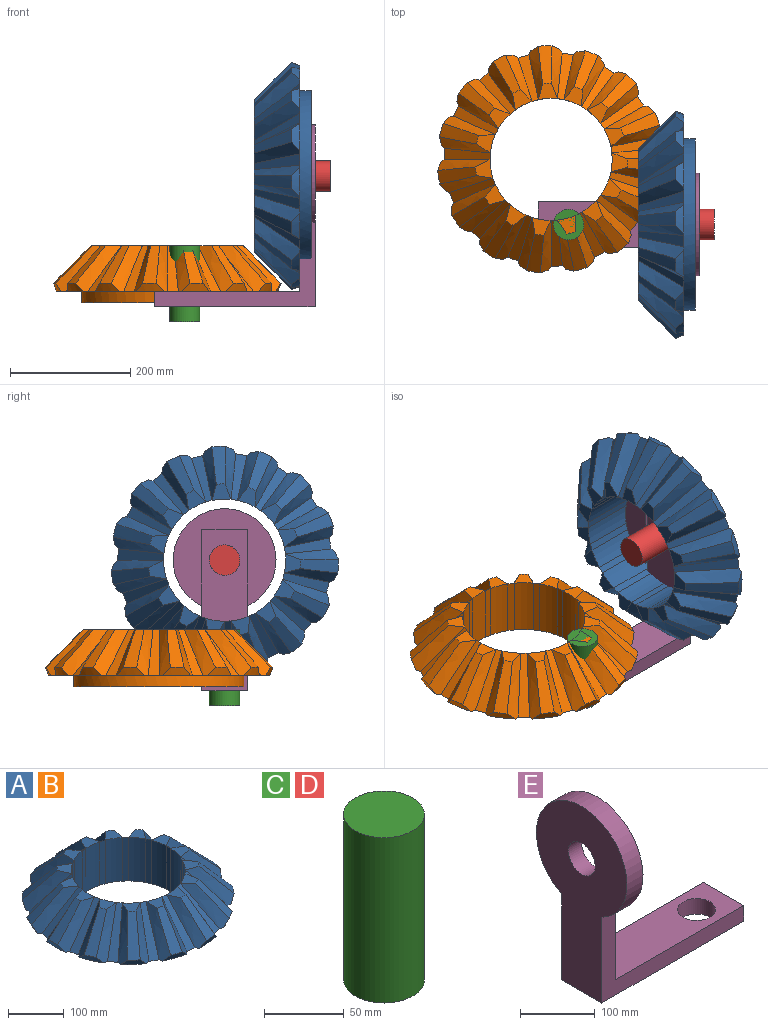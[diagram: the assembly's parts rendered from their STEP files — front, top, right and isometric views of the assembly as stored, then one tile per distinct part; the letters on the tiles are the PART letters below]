
ASSEMBLY  parts=5 mates=5
PART A: 123 faces, bbox 408.6x408.6x95.3 mm
  f0: plane 31.03x30.54mm, normal (0,0,1), area 585.2mm2, adj f44,f46,f50,f92
  f1: plane 31.03x30.54mm, normal (0,0,1), area 585.2mm2, adj f16,f47,f88,f94
  f2: plane 34.9x34.21mm, normal (0,0,1), area 585.2mm2, adj f18,f85,f89,f96
  f3: plane 34.36x33.22mm, normal (0,0,1), area 585.2mm2, adj f20,f82,f86,f98
  f4: plane 31.55x28.57mm, normal (0,0,1), area 585.2mm2, adj f22,f79,f83,f100
  f5: plane 32.17x30.17mm, normal (0,0,1), area 585.2mm2, adj f24,f76,f80,f102
  f6: plane 35.05x34.82mm, normal (0,0,1), area 585.2mm2, adj f26,f73,f77,f104
  f7: plane 33.45x31.87mm, normal (0,0,1), area 585.2mm2, adj f28,f70,f74,f106
  f8: plane 31.72x26.5mm, normal (0,0,1), area 585.2mm2, adj f30,f67,f71,f108
  f9: plane 33.45x31.87mm, normal (0,0,1), area 585.2mm2, adj f32,f64,f68,f110
  f10: plane 35.05x34.82mm, normal (0,0,1), area 585.2mm2, adj f34,f61,f65,f112
  f11: plane 32.17x30.17mm, normal (0,0,1), area 585.2mm2, adj f36,f58,f62,f114
  f12: plane 31.55x28.57mm, normal (0,0,1), area 585.2mm2, adj f38,f55,f59,f116
  f13: plane 34.36x33.22mm, normal (0,0,1), area 585.2mm2, adj f40,f52,f56,f118
  f14: plane 34.9x34.21mm, normal (0,0,1), area 585.2mm2, adj f42,f49,f53,f120
  f15: plane 368.3x367.72mm, normal (0,0,-1), area 40460.3mm2, adj f17,f19,f21,f23,f25,f27,f29,f31
  f16: cone r=203.2mm half-angle=45deg, axis (0,0,-1), area 1668.1mm2, adj f1,f17,f47,f88
  f17: cone r=189.73mm half-angle=22.5deg, axis (0,0,1), area 520mm2, adj f15,f16,f47,f88
  f18: cone r=203.2mm half-angle=45deg, axis (0,0,-1), area 1668.1mm2, adj f2,f19,f85,f89
  f19: cone r=189.73mm half-angle=22.5deg, axis (0,0,1), area 520mm2, adj f15,f18,f85,f89
  f20: cone r=203.2mm half-angle=45deg, axis (0,0,-1), area 1668.1mm2, adj f3,f21,f82,f86
  f21: cone r=189.73mm half-angle=22.5deg, axis (0,0,1), area 520mm2, adj f15,f20,f82,f86
  f22: cone r=203.2mm half-angle=45deg, axis (0,0,-1), area 1668.1mm2, adj f4,f23,f79,f83
  f23: cone r=189.73mm half-angle=22.5deg, axis (0,0,1), area 520mm2, adj f15,f22,f79,f83
  f24: cone r=203.2mm half-angle=45deg, axis (0,0,-1), area 1668.1mm2, adj f5,f25,f76,f80
  f25: cone r=189.73mm half-angle=22.5deg, axis (0,0,1), area 520mm2, adj f15,f24,f76,f80
  f26: cone r=203.2mm half-angle=45deg, axis (0,0,-1), area 1668.1mm2, adj f6,f27,f73,f77
  f27: cone r=189.73mm half-angle=22.5deg, axis (0,0,1), area 520mm2, adj f15,f26,f73,f77
  f28: cone r=203.2mm half-angle=45deg, axis (0,0,-1), area 1668.1mm2, adj f7,f29,f70,f74
  f29: cone r=189.73mm half-angle=22.5deg, axis (0,0,1), area 520mm2, adj f15,f28,f70,f74
  f30: cone r=203.2mm half-angle=45deg, axis (0,0,-1), area 1668.1mm2, adj f8,f31,f67,f71
  f31: cone r=189.73mm half-angle=22.5deg, axis (0,0,1), area 520mm2, adj f15,f30,f67,f71
  f32: cone r=203.2mm half-angle=45deg, axis (0,0,-1), area 1668.1mm2, adj f9,f33,f64,f68
  f33: cone r=189.73mm half-angle=22.5deg, axis (0,0,1), area 520mm2, adj f15,f32,f64,f68
  f34: cone r=203.2mm half-angle=45deg, axis (0,0,-1), area 1668.1mm2, adj f10,f35,f61,f65
  f35: cone r=189.73mm half-angle=22.5deg, axis (0,0,1), area 520mm2, adj f15,f34,f61,f65
  f36: cone r=203.2mm half-angle=45deg, axis (0,0,-1), area 1668.1mm2, adj f11,f37,f58,f62
  f37: cone r=189.73mm half-angle=22.5deg, axis (0,0,1), area 520mm2, adj f15,f36,f58,f62
  f38: cone r=203.2mm half-angle=45deg, axis (0,0,-1), area 1668.1mm2, adj f12,f39,f55,f59
  f39: cone r=189.73mm half-angle=22.5deg, axis (0,0,1), area 520mm2, adj f15,f38,f55,f59
  f40: cone r=203.2mm half-angle=45deg, axis (0,0,-1), area 1668.1mm2, adj f13,f41,f52,f56
  f41: cone r=189.73mm half-angle=22.5deg, axis (0,0,1), area 520mm2, adj f15,f40,f52,f56
  f42: cone r=203.2mm half-angle=45deg, axis (0,0,-1), area 1668.1mm2, adj f14,f43,f49,f53
  f43: cone r=189.73mm half-angle=22.5deg, axis (0,0,1), area 520mm2, adj f15,f42,f49,f53
  f44: cone r=203.2mm half-angle=45deg, axis (0,0,-1), area 1668.1mm2, adj f0,f45,f46,f50
  f45: cone r=189.73mm half-angle=22.5deg, axis (0,0,1), area 520mm2, adj f15,f44,f46,f50
  f46: bspline ~101.6x76.2mm, area 2318.6mm2, adj f0,f15,f44,f45,f48
  f47: bspline ~99.08x76.2mm, area 2314.1mm2, adj f1,f15,f16,f17,f48
  f48: plane 76.2x76.2mm, normal (0.71,0,0.71), area 1594.3mm2, adj f15,f46,f47,f93
  f49: bspline ~81.96x76.2mm, area 2318.6mm2, adj f14,f15,f42,f43,f51
  f50: bspline ~103.67x76.2mm, area 2314.1mm2, adj f0,f15,f44,f45,f51
  f51: plane 76.2x75.63mm, normal (0.65,-0.29,0.71), area 1594.3mm2, adj f15,f49,f50,f91
  f52: bspline ~93.36x76.2mm, area 2318.6mm2, adj f13,f15,f40,f41,f54
  f53: bspline ~87.82x76.2mm, area 2314.1mm2, adj f14,f15,f42,f43,f54
  f54: plane 76.2x66.53mm, normal (0.47,-0.53,0.71), area 1594.3mm2, adj f15,f52,f53,f119
  f55: bspline ~104.88x76.2mm, area 2318.6mm2, adj f12,f15,f38,f39,f57
  f56: bspline ~86.68x76.2mm, area 2314.1mm2, adj f13,f15,f40,f41,f57
  f57: plane 77.04x76.2mm, normal (0.22,-0.67,0.71), area 1594.3mm2, adj f15,f55,f56,f117
  f58: bspline ~98.25x76.2mm, area 2318.6mm2, adj f11,f15,f36,f37,f60
  f59: bspline ~103.83x76.2mm, area 2314.1mm2, adj f12,f15,f38,f39,f60
  f60: plane 77.33x76.2mm, normal (-0.07,-0.7,0.71), area 1594.3mm2, adj f15,f58,f59,f115
  f61: bspline ~76.2x74.64mm, area 2318.6mm2, adj f10,f15,f34,f35,f63
  f62: bspline ~101.33x76.2mm, area 2314.1mm2, adj f11,f15,f36,f37,f63
  f63: plane 76.2x73.39mm, normal (-0.35,-0.61,0.71), area 1594.3mm2, adj f15,f61,f62,f113
  f64: bspline ~97.89x76.2mm, area 2318.6mm2, adj f9,f15,f32,f33,f66
  f65: bspline ~81.31x76.2mm, area 2314.1mm2, adj f10,f15,f34,f35,f66
  f66: plane 76.2x70.34mm, normal (-0.57,-0.42,0.71), area 1594.3mm2, adj f15,f64,f65,f111
  f67: bspline ~104.93x76.2mm, area 2318.6mm2, adj f8,f15,f30,f31,f69
  f68: bspline ~93.83x76.2mm, area 2314.1mm2, adj f9,f15,f32,f33,f69
  f69: plane 77.61x76.2mm, normal (-0.69,-0.15,0.71), area 1594.3mm2, adj f15,f67,f68,f109
  f70: bspline ~93.83x76.2mm, area 2318.6mm2, adj f7,f15,f28,f29,f72
  f71: bspline ~104.93x76.2mm, area 2314.1mm2, adj f8,f15,f30,f31,f72
  f72: plane 77.61x76.2mm, normal (-0.69,0.15,0.71), area 1594.3mm2, adj f15,f70,f71,f107
  f73: bspline ~81.31x76.2mm, area 2318.6mm2, adj f6,f15,f26,f27,f75
  f74: bspline ~97.89x76.2mm, area 2314.1mm2, adj f7,f15,f28,f29,f75
  f75: plane 76.2x70.34mm, normal (-0.57,0.42,0.71), area 1594.3mm2, adj f15,f73,f74,f105
  f76: bspline ~98.03x76.2mm, area 2318.6mm2, adj f5,f15,f24,f25,f78
  f77: bspline ~76.2x74.64mm, area 2314.1mm2, adj f6,f15,f26,f27,f78
  f78: plane 76.2x73.39mm, normal (-0.35,0.61,0.71), area 1594.3mm2, adj f15,f76,f77,f103
  f79: bspline ~101.1x76.2mm, area 2318.6mm2, adj f4,f15,f22,f23,f81
  f80: bspline ~98.25x76.2mm, area 2314.1mm2, adj f5,f15,f24,f25,f81
  f81: plane 77.33x76.2mm, normal (-0.07,0.7,0.71), area 1594.3mm2, adj f15,f79,f80,f101
  f82: bspline ~86.68x76.2mm, area 2318.6mm2, adj f3,f15,f20,f21,f84
  f83: bspline ~104.88x76.2mm, area 2314.1mm2, adj f4,f15,f22,f23,f84
  f84: plane 77.04x76.2mm, normal (0.22,0.67,0.71), area 1594.3mm2, adj f15,f82,f83,f99
  f85: bspline ~87.82x76.2mm, area 2318.6mm2, adj f2,f15,f18,f19,f87
  f86: bspline ~93.36x76.2mm, area 2314.1mm2, adj f3,f15,f20,f21,f87
  f87: plane 76.2x66.53mm, normal (0.47,0.53,0.71), area 1594.3mm2, adj f15,f85,f86,f97
  f88: bspline ~103.67x76.2mm, area 2318.6mm2, adj f1,f15,f16,f17,f90
  f89: bspline ~81.96x76.2mm, area 2314.1mm2, adj f2,f15,f18,f19,f90
  f90: plane 76.2x75.63mm, normal (0.65,0.29,0.71), area 1594.3mm2, adj f15,f88,f89,f95
  f91: plane 95.25x9.83mm, normal (-0.91,0.41,0), area 1024.8mm2, adj f51,f92,f120,f122
  f92: cylinder r=101.74mm len=95.25mm, axis (0,0,1), area 3034mm2, adj f0,f91,f93,f122
  f93: plane 95.25x10.76mm, normal (-1,0,0), area 1024.8mm2, adj f48,f92,f94,f122
  f94: cylinder r=101.74mm len=95.25mm, axis (0,0,1), area 3034mm2, adj f1,f93,f95,f122
  f95: plane 95.25x9.83mm, normal (-0.91,-0.41,0), area 1024.8mm2, adj f90,f94,f96,f122
  f96: cylinder r=101.74mm len=95.25mm, axis (0,0,1), area 3034mm2, adj f2,f95,f97,f122
  f97: plane 95.25x8mm, normal (-0.67,-0.74,0), area 1024.8mm2, adj f87,f96,f98,f122
  f98: cylinder r=101.74mm len=95.25mm, axis (0,0,1), area 3034mm2, adj f3,f97,f99,f122
  f99: plane 95.25x10.23mm, normal (-0.31,-0.95,0), area 1024.8mm2, adj f84,f98,f100,f122
  f100: cylinder r=101.74mm len=95.25mm, axis (0,0,1), area 3034mm2, adj f4,f99,f101,f122
  f101: plane 95.25x10.7mm, normal (0.1,-0.99,0), area 1024.8mm2, adj f81,f100,f102,f122
  f102: cylinder r=101.74mm len=95.25mm, axis (0,0,1), area 3034mm2, adj f5,f101,f103,f122
  f103: plane 95.25x9.32mm, normal (0.5,-0.87,0), area 1024.8mm2, adj f78,f102,f104,f122
  f104: cylinder r=101.74mm len=95.25mm, axis (0,0,1), area 3034mm2, adj f6,f103,f105,f122
  f105: plane 95.25x8.7mm, normal (0.81,-0.59,0), area 1024.8mm2, adj f75,f104,f106,f122
  f106: cylinder r=101.74mm len=95.25mm, axis (0,0,1), area 3034mm2, adj f7,f105,f107,f122
  f107: plane 95.25x10.52mm, normal (0.98,-0.21,0), area 1024.8mm2, adj f72,f106,f108,f122
  f108: cylinder r=101.74mm len=95.25mm, axis (0,0,1), area 3034mm2, adj f8,f107,f109,f122
  f109: plane 95.25x10.52mm, normal (0.98,0.21,0), area 1024.8mm2, adj f69,f108,f110,f122
  f110: cylinder r=101.74mm len=95.25mm, axis (0,0,1), area 3034mm2, adj f9,f109,f111,f122
  f111: plane 95.25x8.7mm, normal (0.81,0.59,0), area 1024.8mm2, adj f66,f110,f112,f122
  f112: cylinder r=101.74mm len=95.25mm, axis (0,0,1), area 3034mm2, adj f10,f111,f113,f122
  f113: plane 95.25x9.32mm, normal (0.5,0.87,0), area 1024.8mm2, adj f63,f112,f114,f122
  f114: cylinder r=101.74mm len=95.25mm, axis (0,0,1), area 3034mm2, adj f11,f113,f115,f122
  f115: plane 95.25x10.7mm, normal (0.1,0.99,0), area 1024.8mm2, adj f60,f114,f116,f122
  f116: cylinder r=101.74mm len=95.25mm, axis (0,0,1), area 3034mm2, adj f12,f115,f117,f122
  f117: plane 95.25x10.23mm, normal (-0.31,0.95,0), area 1024.8mm2, adj f57,f116,f118,f122
  f118: cylinder r=101.74mm len=95.25mm, axis (0,0,1), area 3034mm2, adj f13,f117,f119,f122
  f119: plane 95.25x8mm, normal (-0.67,0.74,0), area 1024.8mm2, adj f54,f118,f120,f122
  f120: cylinder r=101.74mm len=95.25mm, axis (0,0,1), area 3034mm2, adj f14,f91,f119,f122
  f121: cylinder r=142.54mm len=285.08mm, axis (0,0,1), area 17061.4mm2, adj f15,f122
  f122: plane 285.08x285.08mm, normal (0,0,-1), area 31325.5mm2, adj f91,f92,f93,f94,f95,f96,f97,f98
PART B: same geometry as A
PART C: 3 faces, bbox 50.8x50.8x127 mm
  f0: cylinder r=25.4mm len=127mm, axis (0,0,-1), area 20268.3mm2, adj f1,f2
  f1: plane 50.8x50.8mm, normal (0,0,1), area 2026.8mm2, adj f0
  f2: plane 50.8x50.8mm, normal (0,0,-1), area 2026.8mm2, adj f0
PART D: same geometry as C
PART E: 14 faces, bbox 268x171.2x302.8 mm
  f0: plane 302.76x171.19mm, normal (-1,0,0), area 31237.6mm2, adj f1,f5,f6,f8,f12
  f1: plane 267.97x76.2mm, normal (0,0,-1), area 18392.5mm2, adj f0,f2,f5,f6,f7
  f2: plane 76.2x25.4mm, normal (1,0,0), area 1935.5mm2, adj f1,f3,f5,f6
  f3: plane 242.57x76.2mm, normal (0,0,1), area 16457mm2, adj f2,f4,f5,f6,f7
  f4: plane 242.57x76.2mm, normal (1,0,0), area 16457mm2, adj f3,f5,f6,f8,f9,f10,f11
  f5: plane 267.97x140.52mm, normal (0,-1,0), area 9730.6mm2, adj f0,f1,f2,f3,f4,f12
  f6: plane 267.97x140.52mm, normal (0,1,0), area 9730.6mm2, adj f0,f1,f2,f3,f4,f12
  f7: cylinder r=25.4mm len=50.8mm, axis (0,0,1), area 4053.7mm2, adj f1,f3
  f8: cylinder r=25.4mm len=50.8mm, axis (1,0,0), area 4053.7mm2, adj f0,f4
  f9: plane 127.45x4.96mm, normal (0,1,0), area 632.7mm2, adj f4,f11,f12,f13
  f10: plane 127.45x4.96mm, normal (0,-1,0), area 632.7mm2, adj f4,f11,f12,f13
  f11: plane 76.2x4.96mm, normal (0,0,-1), area 378.3mm2, adj f4,f9,f10,f13
  f12: cylinder r=85.59mm len=171.19mm, axis (-1,0,0), area 13932.2mm2, adj f0,f5,f6,f9,f10,f13
  f13: plane 171.19x162.24mm, normal (1,0,0), area 12845.2mm2, adj f9,f10,f11,f12
PLACE A rot(axis=(-0.46,-0.76,0.46),105.8deg) t=(191.77,0,217.17)mm
PLACE B rot(axis=(0,0,-1),63deg) t=(-29.2,108.73,25.4)mm
PLACE C rot(axis=(0,0,1),27deg) t=(0,0,-25.4)mm
PLACE D rot(axis=(-0.7,-0.17,0.7),161deg) t=(242.57,0,217.17)mm
PLACE E rot(axis=(0,0,1),180deg) t=(217.17,0,0)mm
MATE cylindrical E.f7 <-> C.f0  axis (0,0,1) through (0,0,12.7)mm
MATE fastened C.f0 <-> B.f0  axis (0,0,1) through (0,0,101.6)mm
MATE revolute A.f16 <-> E.f8  axis (1,0,0) through (191.77,0,217.17)mm
MATE fastened D.f0 <-> A.f0  axis (-1,0,0) through (115.57,0,217.17)mm
MATE cylindrical E.f8 <-> D.f0  axis (-1,0,0) through (204.47,0,217.17)mm
